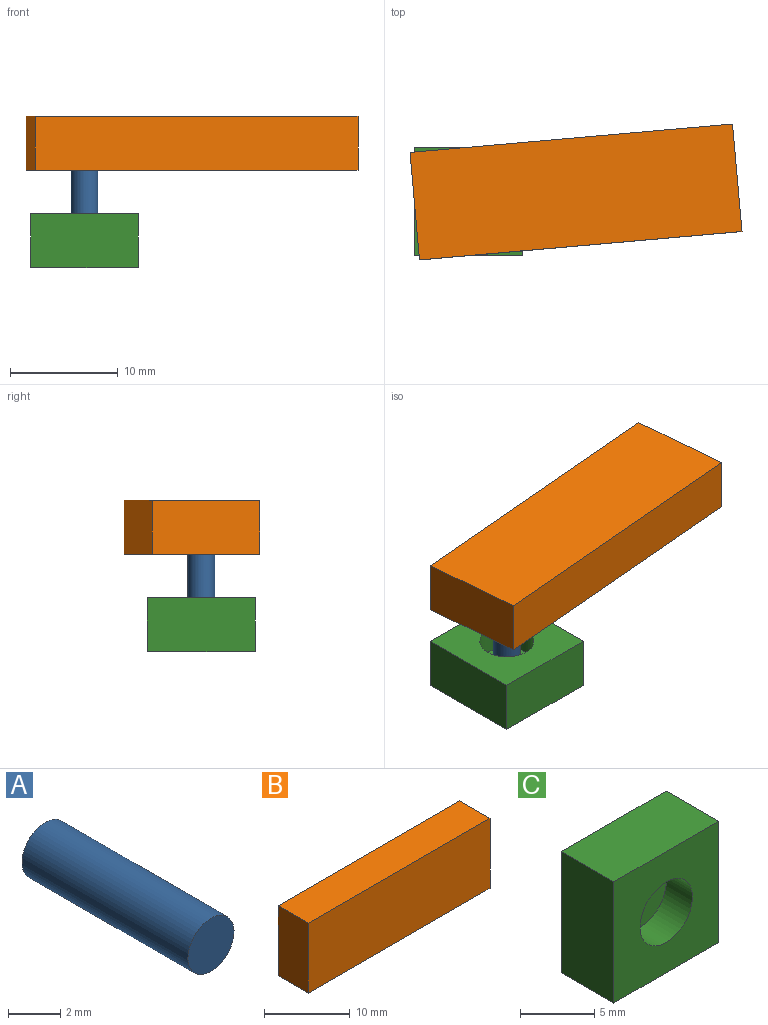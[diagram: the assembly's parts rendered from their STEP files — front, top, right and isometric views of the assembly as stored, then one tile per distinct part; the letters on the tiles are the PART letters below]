
ASSEMBLY  parts=3 mates=2
PART A: 3 faces, bbox 2.5x9x2.5 mm
  f0: cylinder r=1.25mm len=9mm, axis (0,1,0), area 70.7mm2, adj f1,f2
  f1: plane 2.5x2.5mm, normal (0,-1,0), area 4.9mm2, adj f0
  f2: plane 2.5x2.5mm, normal (0,1,0), area 4.9mm2, adj f0
PART B: 8 faces, bbox 30x5x10 mm
  f0: plane 30x5mm, normal (0,0,1), area 150mm2, adj f1,f3,f4,f5
  f1: plane 10x5mm, normal (-1,0,0), area 50mm2, adj f0,f2,f4,f5
  f2: plane 30x5mm, normal (0,0,-1), area 150mm2, adj f1,f3,f4,f5
  f3: plane 10x5mm, normal (1,0,0), area 50mm2, adj f0,f2,f4,f5
  f4: plane 30x10mm, normal (0,-1,0), area 300mm2, adj f0,f1,f2,f3
  f5: plane 30x10mm, normal (0,1,0), area 280.4mm2, adj f0,f1,f2,f3,f6
  f6: cylinder r=2.5mm len=5mm, axis (0,1,0), area 39.3mm2, adj f5,f7
  f7: plane 5x5mm, normal (0,1,0), area 19.6mm2, adj f6
PART C: 8 faces, bbox 10x5x10 mm
  f0: plane 10x5mm, normal (-1,0,0), area 50mm2, adj f1,f3,f4,f5
  f1: plane 10x5mm, normal (0,0,-1), area 50mm2, adj f0,f2,f4,f5
  f2: plane 10x5mm, normal (1,0,0), area 50mm2, adj f1,f3,f4,f5
  f3: plane 10x5mm, normal (0,0,1), area 50mm2, adj f0,f2,f4,f5
  f4: plane 10x10mm, normal (0,-1,0), area 80.4mm2, adj f0,f1,f2,f3,f6
  f5: plane 10x10mm, normal (0,1,0), area 100mm2, adj f0,f1,f2,f3
  f6: cylinder r=2.5mm len=5mm, axis (0,-1,0), area 39.3mm2, adj f4,f7
  f7: plane 5x5mm, normal (0,-1,0), area 19.6mm2, adj f6
PLACE A rot(axis=(-1,0,0),90deg) t=(-25.64,-14.57,2.5)mm
PLACE B rot(axis=(-1,-0.04,0.04),90.1deg) t=(-19.48,-21.05,9)mm
PLACE C rot(axis=(-1,0,0),90deg) t=(-27.24,-22.85,0)mm
MATE revolute A.f0 <-> B.f6  axis (0,0,1) through (0,0,11.5)mm
MATE revolute C.f6 <-> A.f0  axis (0,0,1) through (0,0,2.5)mm
